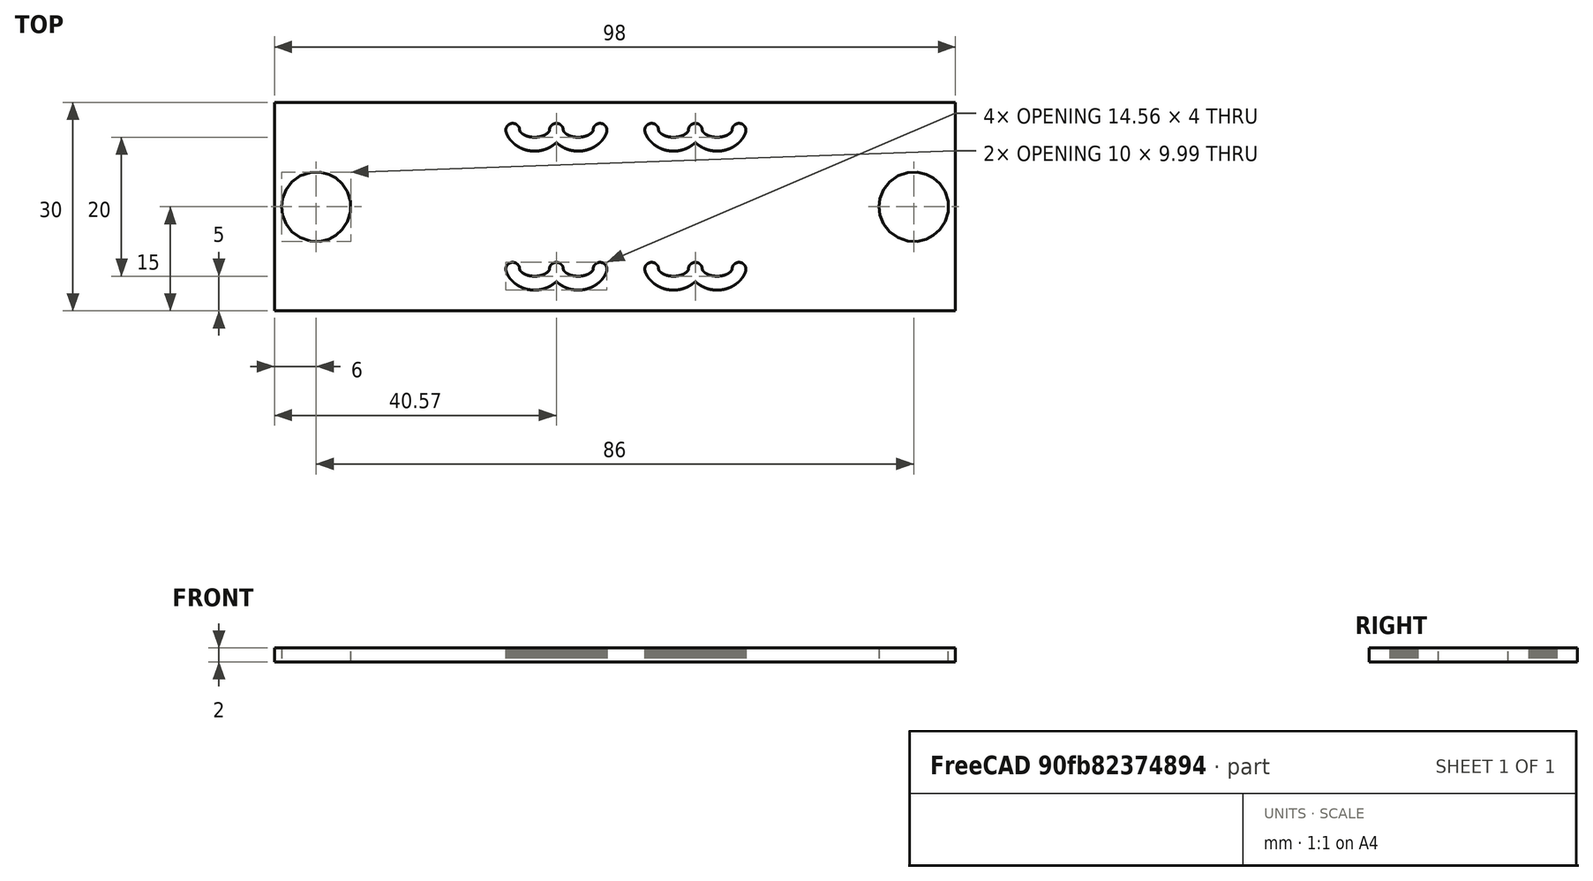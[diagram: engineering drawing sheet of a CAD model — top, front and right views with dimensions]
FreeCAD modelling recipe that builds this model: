
FCSTD DOCUMENT  (FreeCAD 0.21R33771 (Git))
Label: slot
License: All rights reserved
LicenseURL: http://en.wikipedia.org/wiki/All_rights_reserved
objects: Part::Feature×7, PartDesign::CoordinateSystem×2, Sketcher::SketchObject×1, PartDesign::Pad×1, PartDesign::Body×1, App::Part×1, Part::FeaturePython×1
note: 14 computed .brp shape members not serialized (recipe doc carries the construction recipe); baked Part::Feature solids carry a one-line shape summary decoded from their .brp

FEATURE [PartDesign::CoordinateSystem] LCS_0
  AttacherType = Attacher::AttachEngine3D
  MapMode = 2
  Support = -> [X_Axis]
FEATURE [PartDesign::CoordinateSystem] LCS_001
  AttacherType = Attacher::AttachEngine3D
  MapMode = 2
  Support = -> [X_Axis001]
FEATURE [Part::Feature] Rectangle
  shape: bbox 98 x 30 x 2e-07 mm, 0 faces, 0 solids (baked)
FEATURE [Part::Feature] Circle
  Placement = pos=(6,-15,0) rot=(0,0,1;0rad)
  shape: bbox 11.04 x 12.07 x 2e-07 mm, 0 faces, 0 solids (baked)
FEATURE [Part::Feature] Circle001
  Placement = pos=(92,-15,0) rot=(0,0,1;0rad)
  shape: bbox 11.04 x 12.07 x 2e-07 mm, 0 faces, 0 solids (baked)
FEATURE [Part::Feature] Polyline
  shape: bbox 14.56 x 4 x 2e-07 mm, 0 faces, 0 solids (baked)
FEATURE [Part::Feature] Polyline001
  shape: bbox 14.56 x 4 x 2e-07 mm, 0 faces, 0 solids (baked)
FEATURE [Part::Feature] Polyline002
  shape: bbox 14.56 x 4 x 2e-07 mm, 0 faces, 0 solids (baked)
FEATURE [Part::Feature] Polyline003
  shape: bbox 14.56 x 4 x 2e-07 mm, 0 faces, 0 solids (baked)
FEATURE [Sketcher::SketchObject] Sketch
  FullyConstrained = false
  Placement = pos=(0,0,0) rot=(0,0,1;3.14159rad)
  sketch-geometry (1250):
    g0: BSplineCurve PolesCount=2 KnotsCount=2 Degree=1 IsPeriodic=0
    g1: BSplineCurve PolesCount=2 KnotsCount=2 Degree=1 IsPeriodic=0
    g2: BSplineCurve PolesCount=2 KnotsCount=2 Degree=1 IsPeriodic=0
    g3: BSplineCurve PolesCount=2 KnotsCount=2 Degree=1 IsPeriodic=0
    g4: BSplineCurve PolesCount=6 KnotsCount=4 Degree=2 IsPeriodic=1
    g5: BSplineCurve PolesCount=6 KnotsCount=4 Degree=2 IsPeriodic=1
    g6: BSplineCurve PolesCount=2 KnotsCount=2 Degree=1 IsPeriodic=0
    g7: BSplineCurve PolesCount=2 KnotsCount=2 Degree=1 IsPeriodic=0
    g8: BSplineCurve PolesCount=2 KnotsCount=2 Degree=1 IsPeriodic=0
    g9: BSplineCurve PolesCount=2 KnotsCount=2 Degree=1 IsPeriodic=0
    g10: BSplineCurve PolesCount=2 KnotsCount=2 Degree=1 IsPeriodic=0
    g11: BSplineCurve PolesCount=2 KnotsCount=2 Degree=1 IsPeriodic=0
    g12: BSplineCurve PolesCount=2 KnotsCount=2 Degree=1 IsPeriodic=0
    g13: BSplineCurve PolesCount=2 KnotsCount=2 Degree=1 IsPeriodic=0
    g14: BSplineCurve PolesCount=2 KnotsCount=2 Degree=1 IsPeriodic=0
    g15: BSplineCurve PolesCount=2 KnotsCount=2 Degree=1 IsPeriodic=0
    g16: BSplineCurve PolesCount=2 KnotsCount=2 Degree=1 IsPeriodic=0
    g17: BSplineCurve PolesCount=2 KnotsCount=2 Degree=1 IsPeriodic=0
    g18: BSplineCurve PolesCount=2 KnotsCount=2 Degree=1 IsPeriodic=0
    g19: BSplineCurve PolesCount=2 KnotsCount=2 Degree=1 IsPeriodic=0
    g20: BSplineCurve PolesCount=2 KnotsCount=2 Degree=1 IsPeriodic=0
    g21: BSplineCurve PolesCount=2 KnotsCount=2 Degree=1 IsPeriodic=0
    g22: BSplineCurve PolesCount=2 KnotsCount=2 Degree=1 IsPeriodic=0
    g23: BSplineCurve PolesCount=2 KnotsCount=2 Degree=1 IsPeriodic=0
    g24: BSplineCurve PolesCount=2 KnotsCount=2 Degree=1 IsPeriodic=0
    g25: BSplineCurve PolesCount=2 KnotsCount=2 Degree=1 IsPeriodic=0
    g26: BSplineCurve PolesCount=2 KnotsCount=2 Degree=1 IsPeriodic=0
    g27: BSplineCurve PolesCount=2 KnotsCount=2 Degree=1 IsPeriodic=0
    g28: BSplineCurve PolesCount=2 KnotsCount=2 Degree=1 IsPeriodic=0
    g29: BSplineCurve PolesCount=2 KnotsCount=2 Degree=1 IsPeriodic=0
    g30: BSplineCurve PolesCount=2 KnotsCount=2 Degree=1 IsPeriodic=0
    g31: BSplineCurve PolesCount=2 KnotsCount=2 Degree=1 IsPeriodic=0
    g32: BSplineCurve PolesCount=2 KnotsCount=2 Degree=1 IsPeriodic=0
    g33: BSplineCurve PolesCount=2 KnotsCount=2 Degree=1 IsPeriodic=0
    g34: BSplineCurve PolesCount=2 KnotsCount=2 Degree=1 IsPeriodic=0
    g35: BSplineCurve PolesCount=2 KnotsCount=2 Degree=1 IsPeriodic=0
    g36: BSplineCurve PolesCount=2 KnotsCount=2 Degree=1 IsPeriodic=0
    g37: BSplineCurve PolesCount=2 KnotsCount=2 Degree=1 IsPeriodic=0
    g38: BSplineCurve PolesCount=2 KnotsCount=2 Degree=1 IsPeriodic=0
    g39: BSplineCurve PolesCount=2 KnotsCount=2 Degree=1 IsPeriodic=0
    g40: BSplineCurve PolesCount=2 KnotsCount=2 Degree=1 IsPeriodic=0
    g41: BSplineCurve PolesCount=2 KnotsCount=2 Degree=1 IsPeriodic=0
    g42: BSplineCurve PolesCount=2 KnotsCount=2 Degree=1 IsPeriodic=0
    g43: BSplineCurve PolesCount=2 KnotsCount=2 Degree=1 IsPeriodic=0
    g44: BSplineCurve PolesCount=2 KnotsCount=2 Degree=1 IsPeriodic=0
    g45: BSplineCurve PolesCount=2 KnotsCount=2 Degree=1 IsPeriodic=0
    g46: BSplineCurve PolesCount=2 KnotsCount=2 Degree=1 IsPeriodic=0
    g47: BSplineCurve PolesCount=2 KnotsCount=2 Degree=1 IsPeriodic=0
    g48: BSplineCurve PolesCount=2 KnotsCount=2 Degree=1 IsPeriodic=0
    g49: BSplineCurve PolesCount=2 KnotsCount=2 Degree=1 IsPeriodic=0
    g50: BSplineCurve PolesCount=2 KnotsCount=2 Degree=1 IsPeriodic=0
    g51: BSplineCurve PolesCount=2 KnotsCount=2 Degree=1 IsPeriodic=0
    g52: BSplineCurve PolesCount=2 KnotsCount=2 Degree=1 IsPeriodic=0
    g53: BSplineCurve PolesCount=2 KnotsCount=2 Degree=1 IsPeriodic=0
    g54: BSplineCurve PolesCount=2 KnotsCount=2 Degree=1 IsPeriodic=0
    g55: BSplineCurve PolesCount=2 KnotsCount=2 Degree=1 IsPeriodic=0
    g56: BSplineCurve PolesCount=2 KnotsCount=2 Degree=1 IsPeriodic=0
    g57: BSplineCurve PolesCount=2 KnotsCount=2 Degree=1 IsPeriodic=0
    g58: BSplineCurve PolesCount=2 KnotsCount=2 Degree=1 IsPeriodic=0
    g59: BSplineCurve PolesCount=2 KnotsCount=2 Degree=1 IsPeriodic=0
    g60: BSplineCurve PolesCount=2 KnotsCount=2 Degree=1 IsPeriodic=0
    g61: BSplineCurve PolesCount=2 KnotsCount=2 Degree=1 IsPeriodic=0
    g62: BSplineCurve PolesCount=2 KnotsCount=2 Degree=1 IsPeriodic=0
    g63: BSplineCurve PolesCount=2 KnotsCount=2 Degree=1 IsPeriodic=0
    g64: BSplineCurve PolesCount=2 KnotsCount=2 Degree=1 IsPeriodic=0
    g65: BSplineCurve PolesCount=2 KnotsCount=2 Degree=1 IsPeriodic=0
    g66: BSplineCurve PolesCount=2 KnotsCount=2 Degree=1 IsPeriodic=0
    g67: BSplineCurve PolesCount=2 KnotsCount=2 Degree=1 IsPeriodic=0
    g68: BSplineCurve PolesCount=2 KnotsCount=2 Degree=1 IsPeriodic=0
    g69: BSplineCurve PolesCount=2 KnotsCount=2 Degree=1 IsPeriodic=0
    g70: BSplineCurve PolesCount=2 KnotsCount=2 Degree=1 IsPeriodic=0
    g71: BSplineCurve PolesCount=2 KnotsCount=2 Degree=1 IsPeriodic=0
    g72: BSplineCurve PolesCount=2 KnotsCount=2 Degree=1 IsPeriodic=0
    g73: BSplineCurve PolesCount=2 KnotsCount=2 Degree=1 IsPeriodic=0
    g74: BSplineCurve PolesCount=2 KnotsCount=2 Degree=1 IsPeriodic=0
    g75: BSplineCurve PolesCount=2 KnotsCount=2 Degree=1 IsPeriodic=0
    g76: BSplineCurve PolesCount=2 KnotsCount=2 Degree=1 IsPeriodic=0
    g77: BSplineCurve PolesCount=2 KnotsCount=2 Degree=1 IsPeriodic=0
    g78: BSplineCurve PolesCount=2 KnotsCount=2 Degree=1 IsPeriodic=0
    g79: BSplineCurve PolesCount=2 KnotsCount=2 Degree=1 IsPeriodic=0
    g80: BSplineCurve PolesCount=2 KnotsCount=2 Degree=1 IsPeriodic=0
    g81: BSplineCurve PolesCount=2 KnotsCount=2 Degree=1 IsPeriodic=0
    g82: BSplineCurve PolesCount=2 KnotsCount=2 Degree=1 IsPeriodic=0
    g83: BSplineCurve PolesCount=2 KnotsCount=2 Degree=1 IsPeriodic=0
    g84: BSplineCurve PolesCount=2 KnotsCount=2 Degree=1 IsPeriodic=0
    g85: BSplineCurve PolesCount=2 KnotsCount=2 Degree=1 IsPeriodic=0
    g86: BSplineCurve PolesCount=2 KnotsCount=2 Degree=1 IsPeriodic=0
    g87: BSplineCurve PolesCount=2 KnotsCount=2 Degree=1 IsPeriodic=0
    g88: BSplineCurve PolesCount=2 KnotsCount=2 Degree=1 IsPeriodic=0
    g89: BSplineCurve PolesCount=2 KnotsCount=2 Degree=1 IsPeriodic=0
    g90: BSplineCurve PolesCount=2 KnotsCount=2 Degree=1 IsPeriodic=0
    g91: BSplineCurve PolesCount=2 KnotsCount=2 Degree=1 IsPeriodic=0
    g92: BSplineCurve PolesCount=2 KnotsCount=2 Degree=1 IsPeriodic=0
    g93: BSplineCurve PolesCount=2 KnotsCount=2 Degree=1 IsPeriodic=0
    g94: BSplineCurve PolesCount=2 KnotsCount=2 Degree=1 IsPeriodic=0
    g95: BSplineCurve PolesCount=2 KnotsCount=2 Degree=1 IsPeriodic=0
    g96: BSplineCurve PolesCount=2 KnotsCount=2 Degree=1 IsPeriodic=0
    g97: BSplineCurve PolesCount=2 KnotsCount=2 Degree=1 IsPeriodic=0
    g98: BSplineCurve PolesCount=2 KnotsCount=2 Degree=1 IsPeriodic=0
    g99: BSplineCurve PolesCount=2 KnotsCount=2 Degree=1 IsPeriodic=0
    g100: BSplineCurve PolesCount=2 KnotsCount=2 Degree=1 IsPeriodic=0
    g101: BSplineCurve PolesCount=2 KnotsCount=2 Degree=1 IsPeriodic=0
    g102: BSplineCurve PolesCount=2 KnotsCount=2 Degree=1 IsPeriodic=0
    g103: BSplineCurve PolesCount=2 KnotsCount=2 Degree=1 IsPeriodic=0
    g104: BSplineCurve PolesCount=2 KnotsCount=2 Degree=1 IsPeriodic=0
    g105: BSplineCurve PolesCount=2 KnotsCount=2 Degree=1 IsPeriodic=0
    g106: BSplineCurve PolesCount=2 KnotsCount=2 Degree=1 IsPeriodic=0
    g107: BSplineCurve PolesCount=2 KnotsCount=2 Degree=1 IsPeriodic=0
    g108: BSplineCurve PolesCount=2 KnotsCount=2 Degree=1 IsPeriodic=0
    g109: BSplineCurve PolesCount=2 KnotsCount=2 Degree=1 IsPeriodic=0
    g110: BSplineCurve PolesCount=2 KnotsCount=2 Degree=1 IsPeriodic=0
    g111: BSplineCurve PolesCount=2 KnotsCount=2 Degree=1 IsPeriodic=0
    g112: BSplineCurve PolesCount=2 KnotsCount=2 Degree=1 IsPeriodic=0
    g113: BSplineCurve PolesCount=2 KnotsCount=2 Degree=1 IsPeriodic=0
    g114: BSplineCurve PolesCount=2 KnotsCount=2 Degree=1 IsPeriodic=0
    g115: BSplineCurve PolesCount=2 KnotsCount=2 Degree=1 IsPeriodic=0
    g116: BSplineCurve PolesCount=2 KnotsCount=2 Degree=1 IsPeriodic=0
    g117: BSplineCurve PolesCount=2 KnotsCount=2 Degree=1 IsPeriodic=0
    g118: BSplineCurve PolesCount=2 KnotsCount=2 Degree=1 IsPeriodic=0
    g119: BSplineCurve PolesCount=2 KnotsCount=2 Degree=1 IsPeriodic=0
    g120: BSplineCurve PolesCount=2 KnotsCount=2 Degree=1 IsPeriodic=0
    g121: BSplineCurve PolesCount=2 KnotsCount=2 Degree=1 IsPeriodic=0
    g122: BSplineCurve PolesCount=2 KnotsCount=2 Degree=1 IsPeriodic=0
    g123: BSplineCurve PolesCount=2 KnotsCount=2 Degree=1 IsPeriodic=0
    g124: BSplineCurve PolesCount=2 KnotsCount=2 Degree=1 IsPeriodic=0
    g125: BSplineCurve PolesCount=2 KnotsCount=2 Degree=1 IsPeriodic=0
    g126: BSplineCurve PolesCount=2 KnotsCount=2 Degree=1 IsPeriodic=0
    g127: BSplineCurve PolesCount=2 KnotsCount=2 Degree=1 IsPeriodic=0
    g128: BSplineCurve PolesCount=2 KnotsCount=2 Degree=1 IsPeriodic=0
    g129: BSplineCurve PolesCount=2 KnotsCount=2 Degree=1 IsPeriodic=0
    g130: BSplineCurve PolesCount=2 KnotsCount=2 Degree=1 IsPeriodic=0
    g131: BSplineCurve PolesCount=2 KnotsCount=2 Degree=1 IsPeriodic=0
    g132: BSplineCurve PolesCount=2 KnotsCount=2 Degree=1 IsPeriodic=0
    g133: BSplineCurve PolesCount=2 KnotsCount=2 Degree=1 IsPeriodic=0
    g134: BSplineCurve PolesCount=2 KnotsCount=2 Degree=1 IsPeriodic=0
    g135: BSplineCurve PolesCount=2 KnotsCount=2 Degree=1 IsPeriodic=0
    g136: BSplineCurve PolesCount=2 KnotsCount=2 Degree=1 IsPeriodic=0
    g137: BSplineCurve PolesCount=2 KnotsCount=2 Degree=1 IsPeriodic=0
    g138: BSplineCurve PolesCount=2 KnotsCount=2 Degree=1 IsPeriodic=0
    g139: BSplineCurve PolesCount=2 KnotsCount=2 Degree=1 IsPeriodic=0
    g140: BSplineCurve PolesCount=2 KnotsCount=2 Degree=1 IsPeriodic=0
    g141: BSplineCurve PolesCount=2 KnotsCount=2 Degree=1 IsPeriodic=0
    g142: BSplineCurve PolesCount=2 KnotsCount=2 Degree=1 IsPeriodic=0
    g143: BSplineCurve PolesCount=2 KnotsCount=2 Degree=1 IsPeriodic=0
    g144: BSplineCurve PolesCount=2 KnotsCount=2 Degree=1 IsPeriodic=0
    g145: BSplineCurve PolesCount=2 KnotsCount=2 Degree=1 IsPeriodic=0
    g146: BSplineCurve PolesCount=2 KnotsCount=2 Degree=1 IsPeriodic=0
    g147: BSplineCurve PolesCount=2 KnotsCount=2 Degree=1 IsPeriodic=0
    g148: BSplineCurve PolesCount=2 KnotsCount=2 Degree=1 IsPeriodic=0
    g149: BSplineCurve PolesCount=2 KnotsCount=2 Degree=1 IsPeriodic=0
    g150: BSplineCurve PolesCount=2 KnotsCount=2 Degree=1 IsPeriodic=0
    g151: BSplineCurve PolesCount=2 KnotsCount=2 Degree=1 IsPeriodic=0
    g152: BSplineCurve PolesCount=2 KnotsCount=2 Degree=1 IsPeriodic=0
    g153: BSplineCurve PolesCount=2 KnotsCount=2 Degree=1 IsPeriodic=0
    g154: BSplineCurve PolesCount=2 KnotsCount=2 Degree=1 IsPeriodic=0
    g155: BSplineCurve PolesCount=2 KnotsCount=2 Degree=1 IsPeriodic=0
    g156: BSplineCurve PolesCount=2 KnotsCount=2 Degree=1 IsPeriodic=0
    g157: BSplineCurve PolesCount=2 KnotsCount=2 Degree=1 IsPeriodic=0
    g158: BSplineCurve PolesCount=2 KnotsCount=2 Degree=1 IsPeriodic=0
    g159: BSplineCurve PolesCount=2 KnotsCount=2 Degree=1 IsPeriodic=0
    g160: BSplineCurve PolesCount=2 KnotsCount=2 Degree=1 IsPeriodic=0
    g161: BSplineCurve PolesCount=2 KnotsCount=2 Degree=1 IsPeriodic=0
    g162: BSplineCurve PolesCount=2 KnotsCount=2 Degree=1 IsPeriodic=0
    g163: BSplineCurve PolesCount=2 KnotsCount=2 Degree=1 IsPeriodic=0
    g164: BSplineCurve PolesCount=2 KnotsCount=2 Degree=1 IsPeriodic=0
    g165: BSplineCurve PolesCount=2 KnotsCount=2 Degree=1 IsPeriodic=0
    g166: BSplineCurve PolesCount=2 KnotsCount=2 Degree=1 IsPeriodic=0
    g167: BSplineCurve PolesCount=2 KnotsCount=2 Degree=1 IsPeriodic=0
    g168: BSplineCurve PolesCount=2 KnotsCount=2 Degree=1 IsPeriodic=0
    g169: BSplineCurve PolesCount=2 KnotsCount=2 Degree=1 IsPeriodic=0
    g170: BSplineCurve PolesCount=2 KnotsCount=2 Degree=1 IsPeriodic=0
    g171: BSplineCurve PolesCount=2 KnotsCount=2 Degree=1 IsPeriodic=0
    g172: BSplineCurve PolesCount=2 KnotsCount=2 Degree=1 IsPeriodic=0
    g173: BSplineCurve PolesCount=2 KnotsCount=2 Degree=1 IsPeriodic=0
    g174: BSplineCurve PolesCount=2 KnotsCount=2 Degree=1 IsPeriodic=0
    g175: BSplineCurve PolesCount=2 KnotsCount=2 Degree=1 IsPeriodic=0
    g176: BSplineCurve PolesCount=2 KnotsCount=2 Degree=1 IsPeriodic=0
    g177: BSplineCurve PolesCount=2 KnotsCount=2 Degree=1 IsPeriodic=0
    g178: BSplineCurve PolesCount=2 KnotsCount=2 Degree=1 IsPeriodic=0
    g179: BSplineCurve PolesCount=2 KnotsCount=2 Degree=1 IsPeriodic=0
    g180: BSplineCurve PolesCount=2 KnotsCount=2 Degree=1 IsPeriodic=0
    g181: BSplineCurve PolesCount=2 KnotsCount=2 Degree=1 IsPeriodic=0
    g182: BSplineCurve PolesCount=2 KnotsCount=2 Degree=1 IsPeriodic=0
    g183: BSplineCurve PolesCount=2 KnotsCount=2 Degree=1 IsPeriodic=0
    g184: BSplineCurve PolesCount=2 KnotsCount=2 Degree=1 IsPeriodic=0
    g185: BSplineCurve PolesCount=2 KnotsCount=2 Degree=1 IsPeriodic=0
    g186: BSplineCurve PolesCount=2 KnotsCount=2 Degree=1 IsPeriodic=0
    g187: BSplineCurve PolesCount=2 KnotsCount=2 Degree=1 IsPeriodic=0
    g188: BSplineCurve PolesCount=2 KnotsCount=2 Degree=1 IsPeriodic=0
    g189: BSplineCurve PolesCount=2 KnotsCount=2 Degree=1 IsPeriodic=0
    g190: BSplineCurve PolesCount=2 KnotsCount=2 Degree=1 IsPeriodic=0
    g191: BSplineCurve PolesCount=2 KnotsCount=2 Degree=1 IsPeriodic=0
    g192: BSplineCurve PolesCount=2 KnotsCount=2 Degree=1 IsPeriodic=0
    g193: BSplineCurve PolesCount=2 KnotsCount=2 Degree=1 IsPeriodic=0
    g194: BSplineCurve PolesCount=2 KnotsCount=2 Degree=1 IsPeriodic=0
    g195: BSplineCurve PolesCount=2 KnotsCount=2 Degree=1 IsPeriodic=0
    g196: BSplineCurve PolesCount=2 KnotsCount=2 Degree=1 IsPeriodic=0
    g197: BSplineCurve PolesCount=2 KnotsCount=2 Degree=1 IsPeriodic=0
    g198: BSplineCurve PolesCount=2 KnotsCount=2 Degree=1 IsPeriodic=0
    g199: BSplineCurve PolesCount=2 KnotsCount=2 Degree=1 IsPeriodic=0
    g200: BSplineCurve PolesCount=2 KnotsCount=2 Degree=1 IsPeriodic=0
    g201: BSplineCurve PolesCount=2 KnotsCount=2 Degree=1 IsPeriodic=0
    g202: BSplineCurve PolesCount=2 KnotsCount=2 Degree=1 IsPeriodic=0
    g203: BSplineCurve PolesCount=2 KnotsCount=2 Degree=1 IsPeriodic=0
    g204: BSplineCurve PolesCount=2 KnotsCount=2 Degree=1 IsPeriodic=0
    g205: BSplineCurve PolesCount=2 KnotsCount=2 Degree=1 IsPeriodic=0
    g206: BSplineCurve PolesCount=2 KnotsCount=2 Degree=1 IsPeriodic=0
    g207: BSplineCurve PolesCount=2 KnotsCount=2 Degree=1 IsPeriodic=0
    g208: BSplineCurve PolesCount=2 KnotsCount=2 Degree=1 IsPeriodic=0
    g209: BSplineCurve PolesCount=2 KnotsCount=2 Degree=1 IsPeriodic=0
    g210: BSplineCurve PolesCount=2 KnotsCount=2 Degree=1 IsPeriodic=0
    g211: BSplineCurve PolesCount=2 KnotsCount=2 Degree=1 IsPeriodic=0
    g212: BSplineCurve PolesCount=2 KnotsCount=2 Degree=1 IsPeriodic=0
    g213: BSplineCurve PolesCount=2 KnotsCount=2 Degree=1 IsPeriodic=0
    g214: BSplineCurve PolesCount=2 KnotsCount=2 Degree=1 IsPeriodic=0
    g215: BSplineCurve PolesCount=2 KnotsCount=2 Degree=1 IsPeriodic=0
    g216: BSplineCurve PolesCount=2 KnotsCount=2 Degree=1 IsPeriodic=0
    g217: BSplineCurve PolesCount=2 KnotsCount=2 Degree=1 IsPeriodic=0
    g218: BSplineCurve PolesCount=2 KnotsCount=2 Degree=1 IsPeriodic=0
    g219: BSplineCurve PolesCount=2 KnotsCount=2 Degree=1 IsPeriodic=0
    g220: BSplineCurve PolesCount=2 KnotsCount=2 Degree=1 IsPeriodic=0
    g221: BSplineCurve PolesCount=2 KnotsCount=2 Degree=1 IsPeriodic=0
    g222: BSplineCurve PolesCount=2 KnotsCount=2 Degree=1 IsPeriodic=0
    g223: BSplineCurve PolesCount=2 KnotsCount=2 Degree=1 IsPeriodic=0
    g224: BSplineCurve PolesCount=2 KnotsCount=2 Degree=1 IsPeriodic=0
    g225: BSplineCurve PolesCount=2 KnotsCount=2 Degree=1 IsPeriodic=0
    g226: BSplineCurve PolesCount=2 KnotsCount=2 Degree=1 IsPeriodic=0
    g227: BSplineCurve PolesCount=2 KnotsCount=2 Degree=1 IsPeriodic=0
    g228: BSplineCurve PolesCount=2 KnotsCount=2 Degree=1 IsPeriodic=0
    g229: BSplineCurve PolesCount=2 KnotsCount=2 Degree=1 IsPeriodic=0
    g230: BSplineCurve PolesCount=2 KnotsCount=2 Degree=1 IsPeriodic=0
    g231: BSplineCurve PolesCount=2 KnotsCount=2 Degree=1 IsPeriodic=0
    g232: BSplineCurve PolesCount=2 KnotsCount=2 Degree=1 IsPeriodic=0
    g233: BSplineCurve PolesCount=2 KnotsCount=2 Degree=1 IsPeriodic=0
    g234: BSplineCurve PolesCount=2 KnotsCount=2 Degree=1 IsPeriodic=0
    g235: BSplineCurve PolesCount=2 KnotsCount=2 Degree=1 IsPeriodic=0
    g236: BSplineCurve PolesCount=2 KnotsCount=2 Degree=1 IsPeriodic=0
    g237: BSplineCurve PolesCount=2 KnotsCount=2 Degree=1 IsPeriodic=0
    g238: BSplineCurve PolesCount=2 KnotsCount=2 Degree=1 IsPeriodic=0
    g239: BSplineCurve PolesCount=2 KnotsCount=2 Degree=1 IsPeriodic=0
    g240: BSplineCurve PolesCount=2 KnotsCount=2 Degree=1 IsPeriodic=0
    g241: BSplineCurve PolesCount=2 KnotsCount=2 Degree=1 IsPeriodic=0
    g242: BSplineCurve PolesCount=2 KnotsCount=2 Degree=1 IsPeriodic=0
    g243: BSplineCurve PolesCount=2 KnotsCount=2 Degree=1 IsPeriodic=0
    g244: BSplineCurve PolesCount=2 KnotsCount=2 Degree=1 IsPeriodic=0
    g245: BSplineCurve PolesCount=2 KnotsCount=2 Degree=1 IsPeriodic=0
    g246: BSplineCurve PolesCount=2 KnotsCount=2 Degree=1 IsPeriodic=0
    g247: BSplineCurve PolesCount=2 KnotsCount=2 Degree=1 IsPeriodic=0
    g248: BSplineCurve PolesCount=2 KnotsCount=2 Degree=1 IsPeriodic=0
    g249: BSplineCurve PolesCount=2 KnotsCount=2 Degree=1 IsPeriodic=0
    g250: BSplineCurve PolesCount=2 KnotsCount=2 Degree=1 IsPeriodic=0
    g251: BSplineCurve PolesCount=2 KnotsCount=2 Degree=1 IsPeriodic=0
    g252: BSplineCurve PolesCount=2 KnotsCount=2 Degree=1 IsPeriodic=0
    g253: BSplineCurve PolesCount=2 KnotsCount=2 Degree=1 IsPeriodic=0
    g254: BSplineCurve PolesCount=2 KnotsCount=2 Degree=1 IsPeriodic=0
    g255: BSplineCurve PolesCount=2 KnotsCount=2 Degree=1 IsPeriodic=0
    g256: BSplineCurve PolesCount=2 KnotsCount=2 Degree=1 IsPeriodic=0
    g257: BSplineCurve PolesCount=2 KnotsCount=2 Degree=1 IsPeriodic=0
    g258: BSplineCurve PolesCount=2 KnotsCount=2 Degree=1 IsPeriodic=0
    g259: BSplineCurve PolesCount=2 KnotsCount=2 Degree=1 IsPeriodic=0
    g260: BSplineCurve PolesCount=2 KnotsCount=2 Degree=1 IsPeriodic=0
    g261: BSplineCurve PolesCount=2 KnotsCount=2 Degree=1 IsPeriodic=0
    g262: BSplineCurve PolesCount=2 KnotsCount=2 Degree=1 IsPeriodic=0
    g263: BSplineCurve PolesCount=2 KnotsCount=2 Degree=1 IsPeriodic=0
    g264: BSplineCurve PolesCount=2 KnotsCount=2 Degree=1 IsPeriodic=0
    g265: BSplineCurve PolesCount=2 KnotsCount=2 Degree=1 IsPeriodic=0
    g266: BSplineCurve PolesCount=2 KnotsCount=2 Degree=1 IsPeriodic=0
    g267: BSplineCurve PolesCount=2 KnotsCount=2 Degree=1 IsPeriodic=0
    g268: BSplineCurve PolesCount=2 KnotsCount=2 Degree=1 IsPeriodic=0
    g269: BSplineCurve PolesCount=2 KnotsCount=2 Degree=1 IsPeriodic=0
    g270: BSplineCurve PolesCount=2 KnotsCount=2 Degree=1 IsPeriodic=0
    g271: BSplineCurve PolesCount=2 KnotsCount=2 Degree=1 IsPeriodic=0
    g272: BSplineCurve PolesCount=2 KnotsCount=2 Degree=1 IsPeriodic=0
    g273: BSplineCurve PolesCount=2 KnotsCount=2 Degree=1 IsPeriodic=0
    g274: BSplineCurve PolesCount=2 KnotsCount=2 Degree=1 IsPeriodic=0
    g275: BSplineCurve PolesCount=2 KnotsCount=2 Degree=1 IsPeriodic=0
    g276: BSplineCurve PolesCount=2 KnotsCount=2 Degree=1 IsPeriodic=0
    g277: BSplineCurve PolesCount=2 KnotsCount=2 Degree=1 IsPeriodic=0
    g278: BSplineCurve PolesCount=2 KnotsCount=2 Degree=1 IsPeriodic=0
    g279: BSplineCurve PolesCount=2 KnotsCount=2 Degree=1 IsPeriodic=0
    g280: BSplineCurve PolesCount=2 KnotsCount=2 Degree=1 IsPeriodic=0
    g281: BSplineCurve PolesCount=2 KnotsCount=2 Degree=1 IsPeriodic=0
    g282: BSplineCurve PolesCount=2 KnotsCount=2 Degree=1 IsPeriodic=0
    g283: BSplineCurve PolesCount=2 KnotsCount=2 Degree=1 IsPeriodic=0
    g284: BSplineCurve PolesCount=2 KnotsCount=2 Degree=1 IsPeriodic=0
    g285: BSplineCurve PolesCount=2 KnotsCount=2 Degree=1 IsPeriodic=0
    g286: BSplineCurve PolesCount=2 KnotsCount=2 Degree=1 IsPeriodic=0
    g287: BSplineCurve PolesCount=2 KnotsCount=2 Degree=1 IsPeriodic=0
    g288: BSplineCurve PolesCount=2 KnotsCount=2 Degree=1 IsPeriodic=0
    g289: BSplineCurve PolesCount=2 KnotsCount=2 Degree=1 IsPeriodic=0
    g290: BSplineCurve PolesCount=2 KnotsCount=2 Degree=1 IsPeriodic=0
    g291: BSplineCurve PolesCount=2 KnotsCount=2 Degree=1 IsPeriodic=0
    g292: BSplineCurve PolesCount=2 KnotsCount=2 Degree=1 IsPeriodic=0
    g293: BSplineCurve PolesCount=2 KnotsCount=2 Degree=1 IsPeriodic=0
    g294: BSplineCurve PolesCount=2 KnotsCount=2 Degree=1 IsPeriodic=0
    g295: BSplineCurve PolesCount=2 KnotsCount=2 Degree=1 IsPeriodic=0
    g296: BSplineCurve PolesCount=2 KnotsCount=2 Degree=1 IsPeriodic=0
    g297: BSplineCurve PolesCount=2 KnotsCount=2 Degree=1 IsPeriodic=0
    g298: BSplineCurve PolesCount=2 KnotsCount=2 Degree=1 IsPeriodic=0
    g299: BSplineCurve PolesCount=2 KnotsCount=2 Degree=1 IsPeriodic=0
    g300: BSplineCurve PolesCount=2 KnotsCount=2 Degree=1 IsPeriodic=0
    g301: BSplineCurve PolesCount=2 KnotsCount=2 Degree=1 IsPeriodic=0
    g302: BSplineCurve PolesCount=2 KnotsCount=2 Degree=1 IsPeriodic=0
    g303: BSplineCurve PolesCount=2 KnotsCount=2 Degree=1 IsPeriodic=0
    g304: BSplineCurve PolesCount=2 KnotsCount=2 Degree=1 IsPeriodic=0
    g305: BSplineCurve PolesCount=2 KnotsCount=2 Degree=1 IsPeriodic=0
    g306: BSplineCurve PolesCount=2 KnotsCount=2 Degree=1 IsPeriodic=0
    g307: BSplineCurve PolesCount=2 KnotsCount=2 Degree=1 IsPeriodic=0
    g308: BSplineCurve PolesCount=2 KnotsCount=2 Degree=1 IsPeriodic=0
    g309: BSplineCurve PolesCount=2 KnotsCount=2 Degree=1 IsPeriodic=0
    g310: BSplineCurve PolesCount=2 KnotsCount=2 Degree=1 IsPeriodic=0
    g311: BSplineCurve PolesCount=2 KnotsCount=2 Degree=1 IsPeriodic=0
    g312: BSplineCurve PolesCount=2 KnotsCount=2 Degree=1 IsPeriodic=0
    g313: BSplineCurve PolesCount=2 KnotsCount=2 Degree=1 IsPeriodic=0
    g314: BSplineCurve PolesCount=2 KnotsCount=2 Degree=1 IsPeriodic=0
    g315: BSplineCurve PolesCount=2 KnotsCount=2 Degree=1 IsPeriodic=0
    g316: BSplineCurve PolesCount=2 KnotsCount=2 Degree=1 IsPeriodic=0
    g317: BSplineCurve PolesCount=2 KnotsCount=2 Degree=1 IsPeriodic=0
    g318: BSplineCurve PolesCount=2 KnotsCount=2 Degree=1 IsPeriodic=0
    g319: BSplineCurve PolesCount=2 KnotsCount=2 Degree=1 IsPeriodic=0
    g320: BSplineCurve PolesCount=2 KnotsCount=2 Degree=1 IsPeriodic=0
    g321: BSplineCurve PolesCount=2 KnotsCount=2 Degree=1 IsPeriodic=0
    g322: BSplineCurve PolesCount=2 KnotsCount=2 Degree=1 IsPeriodic=0
    g323: BSplineCurve PolesCount=2 KnotsCount=2 Degree=1 IsPeriodic=0
    g324: BSplineCurve PolesCount=2 KnotsCount=2 Degree=1 IsPeriodic=0
    g325: BSplineCurve PolesCount=2 KnotsCount=2 Degree=1 IsPeriodic=0
    g326: BSplineCurve PolesCount=2 KnotsCount=2 Degree=1 IsPeriodic=0
    g327: BSplineCurve PolesCount=2 KnotsCount=2 Degree=1 IsPeriodic=0
    g328: BSplineCurve PolesCount=2 KnotsCount=2 Degree=1 IsPeriodic=0
    g329: BSplineCurve PolesCount=2 KnotsCount=2 Degree=1 IsPeriodic=0
    g330: BSplineCurve PolesCount=2 KnotsCount=2 Degree=1 IsPeriodic=0
    g331: BSplineCurve PolesCount=2 KnotsCount=2 Degree=1 IsPeriodic=0
    g332: BSplineCurve PolesCount=2 KnotsCount=2 Degree=1 IsPeriodic=0
    g333: BSplineCurve PolesCount=2 KnotsCount=2 Degree=1 IsPeriodic=0
    g334: BSplineCurve PolesCount=2 KnotsCount=2 Degree=1 IsPeriodic=0
    g335: BSplineCurve PolesCount=2 KnotsCount=2 Degree=1 IsPeriodic=0
    g336: BSplineCurve PolesCount=2 KnotsCount=2 Degree=1 IsPeriodic=0
    g337: BSplineCurve PolesCount=2 KnotsCount=2 Degree=1 IsPeriodic=0
    g338: BSplineCurve PolesCount=2 KnotsCount=2 Degree=1 IsPeriodic=0
    g339: BSplineCurve PolesCount=2 KnotsCount=2 Degree=1 IsPeriodic=0
    g340: BSplineCurve PolesCount=2 KnotsCount=2 Degree=1 IsPeriodic=0
    g341: BSplineCurve PolesCount=2 KnotsCount=2 Degree=1 IsPeriodic=0
    g342: BSplineCurve PolesCount=2 KnotsCount=2 Degree=1 IsPeriodic=0
    g343: BSplineCurve PolesCount=2 KnotsCount=2 Degree=1 IsPeriodic=0
    g344: BSplineCurve PolesCount=2 KnotsCount=2 Degree=1 IsPeriodic=0
    g345: BSplineCurve PolesCount=2 KnotsCount=2 Degree=1 IsPeriodic=0
    g346: BSplineCurve PolesCount=2 KnotsCount=2 Degree=1 IsPeriodic=0
    g347: BSplineCurve PolesCount=2 KnotsCount=2 Degree=1 IsPeriodic=0
    g348: BSplineCurve PolesCount=2 KnotsCount=2 Degree=1 IsPeriodic=0
    g349: BSplineCurve PolesCount=2 KnotsCount=2 Degree=1 IsPeriodic=0
    g350: BSplineCurve PolesCount=2 KnotsCount=2 Degree=1 IsPeriodic=0
    g351: BSplineCurve PolesCount=2 KnotsCount=2 Degree=1 IsPeriodic=0
    g352: BSplineCurve PolesCount=2 KnotsCount=2 Degree=1 IsPeriodic=0
    g353: BSplineCurve PolesCount=2 KnotsCount=2 Degree=1 IsPeriodic=0
    g354: BSplineCurve PolesCount=2 KnotsCount=2 Degree=1 IsPeriodic=0
    g355: BSplineCurve PolesCount=2 KnotsCount=2 Degree=1 IsPeriodic=0
    g356: BSplineCurve PolesCount=2 KnotsCount=2 Degree=1 IsPeriodic=0
    g357: BSplineCurve PolesCount=2 KnotsCount=2 Degree=1 IsPeriodic=0
    g358: BSplineCurve PolesCount=2 KnotsCount=2 Degree=1 IsPeriodic=0
    g359: BSplineCurve PolesCount=2 KnotsCount=2 Degree=1 IsPeriodic=0
    g360: BSplineCurve PolesCount=2 KnotsCount=2 Degree=1 IsPeriodic=0
    g361: BSplineCurve PolesCount=2 KnotsCount=2 Degree=1 IsPeriodic=0
    g362: BSplineCurve PolesCount=2 KnotsCount=2 Degree=1 IsPeriodic=0
    g363: BSplineCurve PolesCount=2 KnotsCount=2 Degree=1 IsPeriodic=0
    g364: BSplineCurve PolesCount=2 KnotsCount=2 Degree=1 IsPeriodic=0
    g365: BSplineCurve PolesCount=2 KnotsCount=2 Degree=1 IsPeriodic=0
    g366: BSplineCurve PolesCount=2 KnotsCount=2 Degree=1 IsPeriodic=0
    g367: BSplineCurve PolesCount=2 KnotsCount=2 Degree=1 IsPeriodic=0
    g368: BSplineCurve PolesCount=2 KnotsCount=2 Degree=1 IsPeriodic=0
    g369: BSplineCurve PolesCount=2 KnotsCount=2 Degree=1 IsPeriodic=0
    g370: BSplineCurve PolesCount=2 KnotsCount=2 Degree=1 IsPeriodic=0
    g371: BSplineCurve PolesCount=2 KnotsCount=2 Degree=1 IsPeriodic=0
    g372: BSplineCurve PolesCount=2 KnotsCount=2 Degree=1 IsPeriodic=0
    g373: BSplineCurve PolesCount=2 KnotsCount=2 Degree=1 IsPeriodic=0
    g374: BSplineCurve PolesCount=2 KnotsCount=2 Degree=1 IsPeriodic=0
    g375: BSplineCurve PolesCount=2 KnotsCount=2 Degree=1 IsPeriodic=0
    g376: BSplineCurve PolesCount=2 KnotsCount=2 Degree=1 IsPeriodic=0
    g377: BSplineCurve PolesCount=2 KnotsCount=2 Degree=1 IsPeriodic=0
    g378: BSplineCurve PolesCount=2 KnotsCount=2 Degree=1 IsPeriodic=0
    g379: BSplineCurve PolesCount=2 KnotsCount=2 Degree=1 IsPeriodic=0
    g380: BSplineCurve PolesCount=2 KnotsCount=2 Degree=1 IsPeriodic=0
    g381: BSplineCurve PolesCount=2 KnotsCount=2 Degree=1 IsPeriodic=0
    g382: BSplineCurve PolesCount=2 KnotsCount=2 Degree=1 IsPeriodic=0
    g383: BSplineCurve PolesCount=2 KnotsCount=2 Degree=1 IsPeriodic=0
    g384: BSplineCurve PolesCount=2 KnotsCount=2 Degree=1 IsPeriodic=0
    g385: BSplineCurve PolesCount=2 KnotsCount=2 Degree=1 IsPeriodic=0
    g386: BSplineCurve PolesCount=2 KnotsCount=2 Degree=1 IsPeriodic=0
    g387: BSplineCurve PolesCount=2 KnotsCount=2 Degree=1 IsPeriodic=0
    g388: BSplineCurve PolesCount=2 KnotsCount=2 Degree=1 IsPeriodic=0
    g389: BSplineCurve PolesCount=2 KnotsCount=2 Degree=1 IsPeriodic=0
    g390: BSplineCurve PolesCount=2 KnotsCount=2 Degree=1 IsPeriodic=0
    g391: BSplineCurve PolesCount=2 KnotsCount=2 Degree=1 IsPeriodic=0
    g392: BSplineCurve PolesCount=2 KnotsCount=2 Degree=1 IsPeriodic=0
    g393: BSplineCurve PolesCount=2 KnotsCount=2 Degree=1 IsPeriodic=0
    g394: BSplineCurve PolesCount=2 KnotsCount=2 Degree=1 IsPeriodic=0
    g395: BSplineCurve PolesCount=2 KnotsCount=2 Degree=1 IsPeriodic=0
    g396: BSplineCurve PolesCount=2 KnotsCount=2 Degree=1 IsPeriodic=0
    g397: BSplineCurve PolesCount=2 KnotsCount=2 Degree=1 IsPeriodic=0
    g398: BSplineCurve PolesCount=2 KnotsCount=2 Degree=1 IsPeriodic=0
    g399: BSplineCurve PolesCount=2 KnotsCount=2 Degree=1 IsPeriodic=0
    ... +850 more geometry lines
  constraints (1248):
    c: Coincident(g0,g1)
    c: Coincident(g1,g2)
    c: Coincident(g2,g3)
    c: Coincident(g3,g0)
    c: Coincident(g6,g7)
    c: Coincident(g7,g8)
    c: Coincident(g8,g9)
    c: Coincident(g9,g10)
    c: Coincident(g10,g11)
    c: Coincident(g11,g12)
    c: Coincident(g12,g13)
    c: Coincident(g13,g14)
    c: Coincident(g14,g15)
    c: Coincident(g15,g16)
    c: Coincident(g16,g17)
    c: Coincident(g17,g18)
    c: Coincident(g18,g19)
    c: Coincident(g19,g20)
    c: Coincident(g20,g21)
    c: Coincident(g21,g22)
    c: Coincident(g22,g23)
    c: Coincident(g23,g24)
    c: Coincident(g24,g25)
    c: Coincident(g25,g26)
    c: Coincident(g26,g27)
    c: Coincident(g27,g28)
    c: Coincident(g28,g29)
    c: Coincident(g29,g30)
    c: Coincident(g30,g31)
    c: Coincident(g31,g32)
    c: Coincident(g32,g33)
    c: Coincident(g33,g34)
    c: Coincident(g34,g35)
    c: Coincident(g35,g36)
    c: Coincident(g36,g37)
    c: Coincident(g37,g38)
    c: Coincident(g38,g39)
    c: Coincident(g39,g40)
    c: Coincident(g40,g41)
    c: Coincident(g41,g42)
    c: Coincident(g42,g43)
    c: Coincident(g43,g44)
    c: Coincident(g44,g45)
    c: Coincident(g45,g46)
    c: Coincident(g46,g47)
    c: Coincident(g47,g48)
    c: Coincident(g48,g49)
    c: Coincident(g49,g50)
    c: Coincident(g50,g51)
    c: Coincident(g51,g52)
    c: Coincident(g52,g53)
    c: Coincident(g53,g54)
    c: Coincident(g54,g55)
    c: Coincident(g55,g56)
    c: Coincident(g56,g57)
    c: Coincident(g57,g58)
    c: Coincident(g58,g59)
    c: Coincident(g59,g60)
    c: Coincident(g60,g61)
    c: Coincident(g61,g62)
    c: Coincident(g62,g63)
    c: Coincident(g63,g64)
    c: Coincident(g64,g65)
    c: Coincident(g65,g66)
    c: Coincident(g66,g67)
    c: Coincident(g67,g68)
    c: Coincident(g68,g69)
    c: Coincident(g69,g70)
    c: Coincident(g70,g71)
    c: Coincident(g71,g72)
    c: Coincident(g72,g73)
    c: Coincident(g73,g74)
    c: Coincident(g74,g75)
    c: Coincident(g75,g76)
    c: Coincident(g76,g77)
    c: Coincident(g77,g78)
    c: Coincident(g78,g79)
    c: Coincident(g79,g80)
    c: Coincident(g80,g81)
    c: Coincident(g81,g82)
    c: Coincident(g82,g83)
    c: Coincident(g83,g84)
    c: Coincident(g84,g85)
    c: Coincident(g85,g86)
    c: Coincident(g86,g87)
    c: Coincident(g87,g88)
    c: Coincident(g88,g89)
    c: Coincident(g89,g90)
    c: Coincident(g90,g91)
    c: Coincident(g91,g92)
    c: Coincident(g92,g93)
    c: Coincident(g93,g94)
    c: Coincident(g94,g95)
    c: Coincident(g95,g96)
    c: Coincident(g96,g97)
    c: Coincident(g97,g98)
    c: Coincident(g98,g99)
    c: Coincident(g99,g100)
    c: Coincident(g100,g101)
    c: Coincident(g101,g102)
    c: Coincident(g102,g103)
    c: Coincident(g103,g104)
    c: Coincident(g104,g105)
    c: Coincident(g105,g106)
    c: Coincident(g106,g107)
    c: Coincident(g107,g108)
    c: Coincident(g108,g109)
    c: Coincident(g109,g110)
    c: Coincident(g110,g111)
    c: Coincident(g111,g112)
    c: Coincident(g112,g113)
    c: Coincident(g113,g114)
    c: Coincident(g114,g115)
    c: Coincident(g115,g116)
    c: Coincident(g116,g117)
    c: Coincident(g117,g118)
    c: Coincident(g118,g119)
    c: Coincident(g119,g120)
    c: Coincident(g120,g121)
    c: Coincident(g121,g122)
    c: Coincident(g122,g123)
    c: Coincident(g123,g124)
    c: Coincident(g124,g125)
    c: Coincident(g125,g126)
    c: Coincident(g126,g127)
    c: Coincident(g127,g128)
    c: Coincident(g128,g129)
    c: Coincident(g129,g130)
    c: Coincident(g130,g131)
    c: Coincident(g131,g132)
    c: Coincident(g132,g133)
    c: Coincident(g133,g134)
    c: Coincident(g134,g135)
    c: Coincident(g135,g136)
    c: Coincident(g136,g137)
    c: Coincident(g137,g138)
    c: Coincident(g138,g139)
    c: Coincident(g139,g140)
    c: Coincident(g140,g141)
    c: Coincident(g141,g142)
    c: Coincident(g142,g143)
    c: Coincident(g143,g144)
    c: Coincident(g144,g145)
    c: Coincident(g145,g146)
    c: Coincident(g146,g147)
    c: Coincident(g147,g148)
    c: Coincident(g148,g149)
    c: Coincident(g149,g150)
    c: Coincident(g150,g151)
    c: Coincident(g151,g152)
    c: Coincident(g152,g153)
    c: Coincident(g153,g154)
    c: Coincident(g154,g155)
    c: Coincident(g155,g156)
    c: Coincident(g156,g157)
    c: Coincident(g157,g158)
    c: Coincident(g158,g159)
    c: Coincident(g159,g160)
    c: Coincident(g160,g161)
    c: Coincident(g161,g162)
    c: Coincident(g162,g163)
    c: Coincident(g163,g164)
    c: Coincident(g164,g165)
    c: Coincident(g165,g166)
    c: Coincident(g166,g167)
    c: Coincident(g167,g168)
    c: Coincident(g168,g169)
    c: Coincident(g169,g170)
    c: Coincident(g170,g171)
    c: Coincident(g171,g172)
    c: Coincident(g172,g173)
    c: Coincident(g173,g174)
    c: Coincident(g174,g175)
    c: Coincident(g175,g176)
    c: Coincident(g176,g177)
    c: Coincident(g177,g178)
    c: Coincident(g178,g179)
    c: Coincident(g179,g180)
    c: Coincident(g180,g181)
    c: Coincident(g181,g182)
    c: Coincident(g182,g183)
    c: Coincident(g183,g184)
    c: Coincident(g184,g185)
    c: Coincident(g185,g186)
    c: Coincident(g186,g187)
    c: Coincident(g187,g188)
    c: Coincident(g188,g189)
    c: Coincident(g189,g190)
    c: Coincident(g190,g191)
    c: Coincident(g191,g192)
    c: Coincident(g192,g193)
    c: Coincident(g193,g194)
    c: Coincident(g194,g195)
    c: Coincident(g195,g196)
    c: Coincident(g196,g197)
    c: Coincident(g197,g198)
    c: Coincident(g198,g199)
    c: Coincident(g199,g200)
    c: Coincident(g200,g201)
    c: Coincident(g201,g202)
    c: Coincident(g202,g203)
    c: Coincident(g203,g204)
    c: Coincident(g204,g205)
    c: Coincident(g205,g206)
    c: Coincident(g206,g207)
    c: Coincident(g207,g208)
    c: Coincident(g208,g209)
    c: Coincident(g209,g210)
    c: Coincident(g210,g211)
    c: Coincident(g211,g212)
    c: Coincident(g212,g213)
    c: Coincident(g213,g214)
    c: Coincident(g214,g215)
    c: Coincident(g215,g216)
    c: Coincident(g216,g217)
    c: Coincident(g217,g218)
    c: Coincident(g218,g219)
    c: Coincident(g219,g220)
    c: Coincident(g220,g221)
    c: Coincident(g221,g222)
    c: Coincident(g222,g223)
    c: Coincident(g223,g224)
    c: Coincident(g224,g225)
    c: Coincident(g225,g226)
    c: Coincident(g226,g227)
    c: Coincident(g227,g228)
    c: Coincident(g228,g229)
    c: Coincident(g229,g230)
    c: Coincident(g230,g231)
    c: Coincident(g231,g232)
    c: Coincident(g232,g233)
    c: Coincident(g233,g234)
    c: Coincident(g234,g235)
    c: Coincident(g235,g236)
    c: Coincident(g236,g237)
    c: Coincident(g237,g238)
    c: Coincident(g238,g239)
    c: Coincident(g239,g240)
    c: Coincident(g240,g241)
    c: Coincident(g241,g242)
    c: Coincident(g242,g243)
    c: Coincident(g243,g244)
    c: Coincident(g244,g245)
    c: Coincident(g245,g246)
    c: Coincident(g246,g247)
    c: Coincident(g247,g248)
    c: Coincident(g248,g249)
    c: Coincident(g249,g250)
    c: Coincident(g250,g251)
    c: Coincident(g251,g252)
    c: Coincident(g252,g253)
    c: Coincident(g253,g254)
    c: Coincident(g254,g255)
    c: Coincident(g255,g256)
    c: Coincident(g256,g257)
    c: Coincident(g257,g258)
    c: Coincident(g258,g259)
    c: Coincident(g259,g260)
    c: Coincident(g260,g261)
    c: Coincident(g261,g262)
    c: Coincident(g262,g263)
    c: Coincident(g263,g264)
    c: Coincident(g264,g265)
    c: Coincident(g265,g266)
    c: Coincident(g266,g267)
    c: Coincident(g267,g268)
    c: Coincident(g268,g269)
    c: Coincident(g269,g270)
    c: Coincident(g270,g271)
    c: Coincident(g271,g272)
    c: Coincident(g272,g273)
    c: Coincident(g273,g274)
    c: Coincident(g274,g275)
    c: Coincident(g275,g276)
    c: Coincident(g276,g277)
    c: Coincident(g277,g278)
    c: Coincident(g278,g279)
    c: Coincident(g279,g280)
    c: Coincident(g280,g281)
    c: Coincident(g281,g282)
    c: Coincident(g282,g283)
    c: Coincident(g283,g284)
    c: Coincident(g284,g285)
    c: Coincident(g285,g286)
    c: Coincident(g286,g287)
    c: Coincident(g287,g288)
    c: Coincident(g288,g289)
    c: Coincident(g289,g290)
    c: Coincident(g290,g291)
    c: Coincident(g291,g292)
    c: Coincident(g292,g293)
    c: Coincident(g293,g294)
    c: Coincident(g294,g295)
    c: Coincident(g295,g296)
    c: Coincident(g296,g297)
    c: Coincident(g297,g298)
    c: Coincident(g298,g299)
    c: Coincident(g299,g300)
    c: Coincident(g300,g301)
    c: Coincident(g301,g302)
    c: Coincident(g302,g303)
    c: Coincident(g303,g304)
    c: Coincident(g304,g305)
    c: Coincident(g305,g306)
    c: Coincident(g306,g307)
    c: Coincident(g307,g308)
    c: Coincident(g308,g309)
    c: Coincident(g309,g310)
    c: Coincident(g310,g311)
    c: Coincident(g311,g312)
    c: Coincident(g312,g313)
    c: Coincident(g313,g314)
    c: Coincident(g314,g315)
    c: Coincident(g315,g316)
    c: Coincident(g316,g6)
    c: Coincident(g317,g318)
    c: Coincident(g318,g319)
    c: Coincident(g319,g320)
    c: Coincident(g320,g321)
    c: Coincident(g321,g322)
    c: Coincident(g322,g323)
    c: Coincident(g323,g324)
    c: Coincident(g324,g325)
    c: Coincident(g325,g326)
    c: Coincident(g326,g327)
    c: Coincident(g327,g328)
    c: Coincident(g328,g329)
    c: Coincident(g329,g330)
    c: Coincident(g330,g331)
    c: Coincident(g331,g332)
    c: Coincident(g332,g333)
    c: Coincident(g333,g334)
    c: Coincident(g334,g335)
    c: Coincident(g335,g336)
    c: Coincident(g336,g337)
    c: Coincident(g337,g338)
    c: Coincident(g338,g339)
    c: Coincident(g339,g340)
    c: Coincident(g340,g341)
    c: Coincident(g341,g342)
    c: Coincident(g342,g343)
    c: Coincident(g343,g344)
    c: Coincident(g344,g345)
    c: Coincident(g345,g346)
    c: Coincident(g346,g347)
    c: Coincident(g347,g348)
    c: Coincident(g348,g349)
    c: Coincident(g349,g350)
    c: Coincident(g350,g351)
    c: Coincident(g351,g352)
    c: Coincident(g352,g353)
    c: Coincident(g353,g354)
    c: Coincident(g354,g355)
    c: Coincident(g355,g356)
    c: Coincident(g356,g357)
    c: Coincident(g357,g358)
    c: Coincident(g358,g359)
    c: Coincident(g359,g360)
    c: Coincident(g360,g361)
    c: Coincident(g361,g362)
    c: Coincident(g362,g363)
    c: Coincident(g363,g364)
    c: Coincident(g364,g365)
    c: Coincident(g365,g366)
    c: Coincident(g366,g367)
    c: Coincident(g367,g368)
    c: Coincident(g368,g369)
    c: Coincident(g369,g370)
    c: Coincident(g370,g371)
    c: Coincident(g371,g372)
    c: Coincident(g372,g373)
    c: Coincident(g373,g374)
    c: Coincident(g374,g375)
    c: Coincident(g375,g376)
    c: Coincident(g376,g377)
    c: Coincident(g377,g378)
    c: Coincident(g378,g379)
    c: Coincident(g379,g380)
    c: Coincident(g380,g381)
    c: Coincident(g381,g382)
    c: Coincident(g382,g383)
    c: Coincident(g383,g384)
    c: Coincident(g384,g385)
    c: Coincident(g385,g386)
    c: Coincident(g386,g387)
    c: Coincident(g387,g388)
    c: Coincident(g388,g389)
    c: Coincident(g389,g390)
    c: Coincident(g390,g391)
    c: Coincident(g391,g392)
    c: Coincident(g392,g393)
    c: Coincident(g393,g394)
    c: Coincident(g394,g395)
    c: Coincident(g395,g396)
    c: Coincident(g396,g397)
    c: Coincident(g397,g398)
    c: Coincident(g398,g399)
    c: Coincident(g399,g400)
    c: Coincident(g400,g401)
    c: Coincident(g401,g402)
    c: Coincident(g402,g403)
    c: Coincident(g403,g404)
    c: Coincident(g404,g405)
    c: Coincident(g405,g406)
    c: Coincident(g406,g407)
    c: Coincident(g407,g408)
    c: Coincident(g408,g409)
    c: Coincident(g409,g410)
    c: Coincident(g410,g411)
    c: Coincident(g411,g412)
    c: Coincident(g412,g413)
    c: Coincident(g413,g414)
    c: Coincident(g414,g415)
    c: Coincident(g415,g416)
    c: Coincident(g416,g417)
    c: Coincident(g417,g418)
    c: Coincident(g418,g419)
    c: Coincident(g419,g420)
    c: Coincident(g420,g421)
    c: Coincident(g421,g422)
    c: Coincident(g422,g423)
    c: Coincident(g423,g424)
    c: Coincident(g424,g425)
    c: Coincident(g425,g426)
    c: Coincident(g426,g427)
    c: Coincident(g427,g428)
    c: Coincident(g428,g429)
    c: Coincident(g429,g430)
    c: Coincident(g430,g431)
    c: Coincident(g431,g432)
    c: Coincident(g432,g433)
    c: Coincident(g433,g434)
    c: Coincident(g434,g435)
    c: Coincident(g435,g436)
    c: Coincident(g436,g437)
    c: Coincident(g437,g438)
    c: Coincident(g438,g439)
    c: Coincident(g439,g440)
    c: Coincident(g440,g441)
    c: Coincident(g441,g442)
    c: Coincident(g442,g443)
    c: Coincident(g443,g444)
    c: Coincident(g444,g445)
    c: Coincident(g445,g446)
    c: Coincident(g446,g447)
    c: Coincident(g447,g448)
    c: Coincident(g448,g449)
    c: Coincident(g449,g450)
    c: Coincident(g450,g451)
    c: Coincident(g451,g452)
    c: Coincident(g452,g453)
    c: Coincident(g453,g454)
    c: Coincident(g454,g455)
    c: Coincident(g455,g456)
    c: Coincident(g456,g457)
    c: Coincident(g457,g458)
    c: Coincident(g458,g459)
    c: Coincident(g459,g460)
    c: Coincident(g460,g461)
    c: Coincident(g461,g462)
    c: Coincident(g462,g463)
    c: Coincident(g463,g464)
    c: Coincident(g464,g465)
    c: Coincident(g465,g466)
    c: Coincident(g466,g467)
    c: Coincident(g467,g468)
    c: Coincident(g468,g469)
    c: Coincident(g469,g470)
    c: Coincident(g470,g471)
    c: Coincident(g471,g472)
    c: Coincident(g472,g473)
    c: Coincident(g473,g474)
    c: Coincident(g474,g475)
    c: Coincident(g475,g476)
    c: Coincident(g476,g477)
    c: Coincident(g477,g478)
    c: Coincident(g478,g479)
    c: Coincident(g479,g480)
    c: Coincident(g480,g481)
    c: Coincident(g481,g482)
    c: Coincident(g482,g483)
    c: Coincident(g483,g484)
    c: Coincident(g484,g485)
    c: Coincident(g485,g486)
    c: Coincident(g486,g487)
    c: Coincident(g487,g488)
    c: Coincident(g488,g489)
    c: Coincident(g489,g490)
    c: Coincident(g490,g491)
    c: Coincident(g491,g492)
    c: Coincident(g492,g493)
    c: Coincident(g493,g494)
    c: Coincident(g494,g495)
    c: Coincident(g495,g496)
    c: Coincident(g496,g497)
    c: Coincident(g497,g498)
    c: Coincident(g498,g499)
    c: Coincident(g499,g500)
    c: Coincident(g500,g501)
    c: Coincident(g501,g502)
    c: Coincident(g502,g503)
    c: Coincident(g503,g504)
    c: Coincident(g504,g505)
    c: Coincident(g505,g506)
    c: Coincident(g506,g507)
    c: Coincident(g507,g508)
    c: Coincident(g508,g509)
    c: Coincident(g509,g510)
    c: Coincident(g510,g511)
    c: Coincident(g511,g512)
    c: Coincident(g512,g513)
    c: Coincident(g513,g514)
    c: Coincident(g514,g515)
    c: Coincident(g515,g516)
    c: Coincident(g516,g517)
    c: Coincident(g517,g518)
    c: Coincident(g518,g519)
    c: Coincident(g519,g520)
    c: Coincident(g520,g521)
    c: Coincident(g521,g522)
    c: Coincident(g522,g523)
    c: Coincident(g523,g524)
    c: Coincident(g524,g525)
    c: Coincident(g525,g526)
    c: Coincident(g526,g527)
    c: Coincident(g527,g528)
    c: Coincident(g528,g529)
    c: Coincident(g529,g530)
    c: Coincident(g530,g531)
    c: Coincident(g531,g532)
    c: Coincident(g532,g533)
    c: Coincident(g533,g534)
    c: Coincident(g534,g535)
    c: Coincident(g535,g536)
    c: Coincident(g536,g537)
    c: Coincident(g537,g538)
    c: Coincident(g538,g539)
    c: Coincident(g539,g540)
    c: Coincident(g540,g541)
    c: Coincident(g541,g542)
    c: Coincident(g542,g543)
    c: Coincident(g543,g544)
    c: Coincident(g544,g545)
    c: Coincident(g545,g546)
    c: Coincident(g546,g547)
    c: Coincident(g547,g548)
    c: Coincident(g548,g549)
    c: Coincident(g549,g550)
    c: Coincident(g550,g551)
    c: Coincident(g551,g552)
    c: Coincident(g552,g553)
    c: Coincident(g553,g554)
    c: Coincident(g554,g555)
    c: Coincident(g555,g556)
    c: Coincident(g556,g557)
    c: Coincident(g557,g558)
    c: Coincident(g558,g559)
    c: Coincident(g559,g560)
    c: Coincident(g560,g561)
    c: Coincident(g561,g562)
    c: Coincident(g562,g563)
    c: Coincident(g563,g564)
    c: Coincident(g564,g565)
    c: Coincident(g565,g566)
    c: Coincident(g566,g567)
    c: Coincident(g567,g568)
    c: Coincident(g568,g569)
    c: Coincident(g569,g570)
    c: Coincident(g570,g571)
    c: Coincident(g571,g572)
    c: Coincident(g572,g573)
    c: Coincident(g573,g574)
    c: Coincident(g574,g575)
    c: Coincident(g575,g576)
    c: Coincident(g576,g577)
    c: Coincident(g577,g578)
    c: Coincident(g578,g579)
    c: Coincident(g579,g580)
    c: Coincident(g580,g581)
    c: Coincident(g581,g582)
    c: Coincident(g582,g583)
    c: Coincident(g583,g584)
    c: Coincident(g584,g585)
    c: Coincident(g585,g586)
    c: Coincident(g586,g587)
    c: Coincident(g587,g588)
    c: Coincident(g588,g589)
    c: Coincident(g589,g590)
    c: Coincident(g590,g591)
    c: Coincident(g591,g592)
    c: Coincident(g592,g593)
    c: Coincident(g593,g594)
    c: Coincident(g594,g595)
    c: Coincident(g595,g596)
    c: Coincident(g596,g597)
    c: Coincident(g597,g598)
    c: Coincident(g598,g599)
    c: Coincident(g599,g600)
    c: Coincident(g600,g601)
    c: Coincident(g601,g602)
    c: Coincident(g602,g603)
    c: Coincident(g603,g604)
    c: Coincident(g604,g605)
    c: Coincident(g605,g606)
    c: Coincident(g606,g607)
    c: Coincident(g607,g608)
    c: Coincident(g608,g609)
    c: Coincident(g609,g610)
    c: Coincident(g610,g611)
    c: Coincident(g611,g612)
    c: Coincident(g612,g613)
    c: Coincident(g613,g614)
    c: Coincident(g614,g615)
    c: Coincident(g615,g616)
    c: Coincident(g616,g617)
    c: Coincident(g617,g618)
    c: Coincident(g618,g619)
    c: Coincident(g619,g620)
    c: Coincident(g620,g621)
    c: Coincident(g621,g622)
    c: Coincident(g622,g623)
    c: Coincident(g623,g624)
    c: Coincident(g624,g625)
    c: Coincident(g625,g626)
    c: Coincident(g626,g627)
    c: Coincident(g627,g317)
    c: Coincident(g628,g629)
    c: Coincident(g629,g630)
    c: Coincident(g630,g631)
    c: Coincident(g631,g632)
    c: Coincident(g632,g633)
    c: Coincident(g633,g634)
    c: Coincident(g634,g635)
    c: Coincident(g635,g636)
    c: Coincident(g636,g637)
    c: Coincident(g637,g638)
    c: Coincident(g638,g639)
    c: Coincident(g639,g640)
    c: Coincident(g640,g641)
    c: Coincident(g641,g642)
    c: Coincident(g642,g643)
    c: Coincident(g643,g644)
    c: Coincident(g644,g645)
    c: Coincident(g645,g646)
    c: Coincident(g646,g647)
    c: Coincident(g647,g648)
    c: Coincident(g648,g649)
    c: Coincident(g649,g650)
    c: Coincident(g650,g651)
    c: Coincident(g651,g652)
    c: Coincident(g652,g653)
    c: Coincident(g653,g654)
    c: Coincident(g654,g655)
    c: Coincident(g655,g656)
    c: Coincident(g656,g657)
    c: Coincident(g657,g658)
    c: Coincident(g658,g659)
    c: Coincident(g659,g660)
    c: Coincident(g660,g661)
    c: Coincident(g661,g662)
    c: Coincident(g662,g663)
    c: Coincident(g663,g664)
    c: Coincident(g664,g665)
    c: Coincident(g665,g666)
    c: Coincident(g666,g667)
    c: Coincident(g667,g668)
    c: Coincident(g668,g669)
    c: Coincident(g669,g670)
    c: Coincident(g670,g671)
    c: Coincident(g671,g672)
    c: Coincident(g672,g673)
    c: Coincident(g673,g674)
    c: Coincident(g674,g675)
    c: Coincident(g675,g676)
    c: Coincident(g676,g677)
    c: Coincident(g677,g678)
    c: Coincident(g678,g679)
    c: Coincident(g679,g680)
    c: Coincident(g680,g681)
    c: Coincident(g681,g682)
    c: Coincident(g682,g683)
    c: Coincident(g683,g684)
    c: Coincident(g684,g685)
    c: Coincident(g685,g686)
    c: Coincident(g686,g687)
    c: Coincident(g687,g688)
    c: Coincident(g688,g689)
    c: Coincident(g689,g690)
    c: Coincident(g690,g691)
    c: Coincident(g691,g692)
    c: Coincident(g692,g693)
    c: Coincident(g693,g694)
    c: Coincident(g694,g695)
    c: Coincident(g695,g696)
    c: Coincident(g696,g697)
    c: Coincident(g697,g698)
    c: Coincident(g698,g699)
    c: Coincident(g699,g700)
    c: Coincident(g700,g701)
    c: Coincident(g701,g702)
    c: Coincident(g702,g703)
    c: Coincident(g703,g704)
    c: Coincident(g704,g705)
    c: Coincident(g705,g706)
    c: Coincident(g706,g707)
    c: Coincident(g707,g708)
    c: Coincident(g708,g709)
    c: Coincident(g709,g710)
    c: Coincident(g710,g711)
    c: Coincident(g711,g712)
    c: Coincident(g712,g713)
    c: Coincident(g713,g714)
    c: Coincident(g714,g715)
    c: Coincident(g715,g716)
    c: Coincident(g716,g717)
    c: Coincident(g717,g718)
    c: Coincident(g718,g719)
    c: Coincident(g719,g720)
    c: Coincident(g720,g721)
    c: Coincident(g721,g722)
    c: Coincident(g722,g723)
    c: Coincident(g723,g724)
    c: Coincident(g724,g725)
    c: Coincident(g725,g726)
    c: Coincident(g726,g727)
    c: Coincident(g727,g728)
    c: Coincident(g728,g729)
    c: Coincident(g729,g730)
    c: Coincident(g730,g731)
    c: Coincident(g731,g732)
    c: Coincident(g732,g733)
    c: Coincident(g733,g734)
    c: Coincident(g734,g735)
    c: Coincident(g735,g736)
    c: Coincident(g736,g737)
    c: Coincident(g737,g738)
    c: Coincident(g738,g739)
    c: Coincident(g739,g740)
    c: Coincident(g740,g741)
    c: Coincident(g741,g742)
    c: Coincident(g742,g743)
    c: Coincident(g743,g744)
    c: Coincident(g744,g745)
    c: Coincident(g745,g746)
    c: Coincident(g746,g747)
    c: Coincident(g747,g748)
    c: Coincident(g748,g749)
    c: Coincident(g749,g750)
    c: Coincident(g750,g751)
    c: Coincident(g751,g752)
    c: Coincident(g752,g753)
    c: Coincident(g753,g754)
    c: Coincident(g754,g755)
    c: Coincident(g755,g756)
    c: Coincident(g756,g757)
    c: Coincident(g757,g758)
    c: Coincident(g758,g759)
    c: Coincident(g759,g760)
    c: Coincident(g760,g761)
    c: Coincident(g761,g762)
    c: Coincident(g762,g763)
    c: Coincident(g763,g764)
    c: Coincident(g764,g765)
    c: Coincident(g765,g766)
    c: Coincident(g766,g767)
    c: Coincident(g767,g768)
    c: Coincident(g768,g769)
    c: Coincident(g769,g770)
    c: Coincident(g770,g771)
    c: Coincident(g771,g772)
    c: Coincident(g772,g773)
    c: Coincident(g773,g774)
    c: Coincident(g774,g775)
    c: Coincident(g775,g776)
    c: Coincident(g776,g777)
    c: Coincident(g777,g778)
    c: Coincident(g778,g779)
    c: Coincident(g779,g780)
    c: Coincident(g780,g781)
    c: Coincident(g781,g782)
    c: Coincident(g782,g783)
    c: Coincident(g783,g784)
    c: Coincident(g784,g785)
    c: Coincident(g785,g786)
    c: Coincident(g786,g787)
    c: Coincident(g787,g788)
    c: Coincident(g788,g789)
    c: Coincident(g789,g790)
    c: Coincident(g790,g791)
    c: Coincident(g791,g792)
    c: Coincident(g792,g793)
    c: Coincident(g793,g794)
    c: Coincident(g794,g795)
    c: Coincident(g795,g796)
    c: Coincident(g796,g797)
    c: Coincident(g797,g798)
    c: Coincident(g798,g799)
    c: Coincident(g799,g800)
    c: Coincident(g800,g801)
    c: Coincident(g801,g802)
    c: Coincident(g802,g803)
    c: Coincident(g803,g804)
    c: Coincident(g804,g805)
    c: Coincident(g805,g806)
    c: Coincident(g806,g807)
    c: Coincident(g807,g808)
    c: Coincident(g808,g809)
    c: Coincident(g809,g810)
    c: Coincident(g810,g811)
    c: Coincident(g811,g812)
    c: Coincident(g812,g813)
    c: Coincident(g813,g814)
    c: Coincident(g814,g815)
    c: Coincident(g815,g816)
    c: Coincident(g816,g817)
    c: Coincident(g817,g818)
    c: Coincident(g818,g819)
    c: Coincident(g819,g820)
    c: Coincident(g820,g821)
    c: Coincident(g821,g822)
    c: Coincident(g822,g823)
    c: Coincident(g823,g824)
    c: Coincident(g824,g825)
    c: Coincident(g825,g826)
    c: Coincident(g826,g827)
    c: Coincident(g827,g828)
    c: Coincident(g828,g829)
    c: Coincident(g829,g830)
    c: Coincident(g830,g831)
    c: Coincident(g831,g832)
    c: Coincident(g832,g833)
    c: Coincident(g833,g834)
    c: Coincident(g834,g835)
    c: Coincident(g835,g836)
    c: Coincident(g836,g837)
    c: Coincident(g837,g838)
    c: Coincident(g838,g839)
    c: Coincident(g839,g840)
    c: Coincident(g840,g841)
    c: Coincident(g841,g842)
    c: Coincident(g842,g843)
    c: Coincident(g843,g844)
    c: Coincident(g844,g845)
    c: Coincident(g845,g846)
    c: Coincident(g846,g847)
    c: Coincident(g847,g848)
    c: Coincident(g848,g849)
    c: Coincident(g849,g850)
    c: Coincident(g850,g851)
    c: Coincident(g851,g852)
    c: Coincident(g852,g853)
    c: Coincident(g853,g854)
    c: Coincident(g854,g855)
    c: Coincident(g855,g856)
    c: Coincident(g856,g857)
    c: Coincident(g857,g858)
    c: Coincident(g858,g859)
    c: Coincident(g859,g860)
    c: Coincident(g860,g861)
    c: Coincident(g861,g862)
    c: Coincident(g862,g863)
    c: Coincident(g863,g864)
    c: Coincident(g864,g865)
    c: Coincident(g865,g866)
    c: Coincident(g866,g867)
    c: Coincident(g867,g868)
    c: Coincident(g868,g869)
    c: Coincident(g869,g870)
    c: Coincident(g870,g871)
    c: Coincident(g871,g872)
    c: Coincident(g872,g873)
    c: Coincident(g873,g874)
    c: Coincident(g874,g875)
    c: Coincident(g875,g876)
    c: Coincident(g876,g877)
    c: Coincident(g877,g878)
    c: Coincident(g878,g879)
    c: Coincident(g879,g880)
    c: Coincident(g880,g881)
    c: Coincident(g881,g882)
    c: Coincident(g882,g883)
    c: Coincident(g883,g884)
    c: Coincident(g884,g885)
    c: Coincident(g885,g886)
    c: Coincident(g886,g887)
    c: Coincident(g887,g888)
    c: Coincident(g888,g889)
    c: Coincident(g889,g890)
    c: Coincident(g890,g891)
    c: Coincident(g891,g892)
    c: Coincident(g892,g893)
    c: Coincident(g893,g894)
    c: Coincident(g894,g895)
    c: Coincident(g895,g896)
    c: Coincident(g896,g897)
    c: Coincident(g897,g898)
    c: Coincident(g898,g899)
    c: Coincident(g899,g900)
    c: Coincident(g900,g901)
    c: Coincident(g901,g902)
    c: Coincident(g902,g903)
    c: Coincident(g903,g904)
    c: Coincident(g904,g905)
    c: Coincident(g905,g906)
    c: Coincident(g906,g907)
    c: Coincident(g907,g908)
    c: Coincident(g908,g909)
    c: Coincident(g909,g910)
    c: Coincident(g910,g911)
    c: Coincident(g911,g912)
    c: Coincident(g912,g913)
    c: Coincident(g913,g914)
    c: Coincident(g914,g915)
    c: Coincident(g915,g916)
    c: Coincident(g916,g917)
    c: Coincident(g917,g918)
    c: Coincident(g918,g919)
    c: Coincident(g919,g920)
    c: Coincident(g920,g921)
    c: Coincident(g921,g922)
    c: Coincident(g922,g923)
    c: Coincident(g923,g924)
    c: Coincident(g924,g925)
    c: Coincident(g925,g926)
    c: Coincident(g926,g927)
    c: Coincident(g927,g928)
    c: Coincident(g928,g929)
    c: Coincident(g929,g930)
    c: Coincident(g930,g931)
    c: Coincident(g931,g932)
    c: Coincident(g932,g933)
    c: Coincident(g933,g934)
    c: Coincident(g934,g935)
    c: Coincident(g935,g936)
    c: Coincident(g936,g937)
    c: Coincident(g937,g938)
    c: Coincident(g938,g628)
    c: Coincident(g939,g940)
    c: Coincident(g940,g941)
    c: Coincident(g941,g942)
    c: Coincident(g942,g943)
    c: Coincident(g943,g944)
    c: Coincident(g944,g945)
    c: Coincident(g945,g946)
    c: Coincident(g946,g947)
    c: Coincident(g947,g948)
    c: Coincident(g948,g949)
    c: Coincident(g949,g950)
    c: Coincident(g950,g951)
    c: Coincident(g951,g952)
    c: Coincident(g952,g953)
    c: Coincident(g953,g954)
    c: Coincident(g954,g955)
    c: Coincident(g955,g956)
    c: Coincident(g956,g957)
    c: Coincident(g957,g958)
    c: Coincident(g958,g959)
    c: Coincident(g959,g960)
    c: Coincident(g960,g961)
    c: Coincident(g961,g962)
    c: Coincident(g962,g963)
    c: Coincident(g963,g964)
    c: Coincident(g964,g965)
    c: Coincident(g965,g966)
    c: Coincident(g966,g967)
    c: Coincident(g967,g968)
    c: Coincident(g968,g969)
    c: Coincident(g969,g970)
    c: Coincident(g970,g971)
    c: Coincident(g971,g972)
    c: Coincident(g972,g973)
    c: Coincident(g973,g974)
    c: Coincident(g974,g975)
    c: Coincident(g975,g976)
    c: Coincident(g976,g977)
    c: Coincident(g977,g978)
    c: Coincident(g978,g979)
    c: Coincident(g979,g980)
    c: Coincident(g980,g981)
    c: Coincident(g981,g982)
    c: Coincident(g982,g983)
    c: Coincident(g983,g984)
    c: Coincident(g984,g985)
    c: Coincident(g985,g986)
    c: Coincident(g986,g987)
    c: Coincident(g987,g988)
    c: Coincident(g988,g989)
    c: Coincident(g989,g990)
    c: Coincident(g990,g991)
    c: Coincident(g991,g992)
    c: Coincident(g992,g993)
    c: Coincident(g993,g994)
    c: Coincident(g994,g995)
    c: Coincident(g995,g996)
    c: Coincident(g996,g997)
    c: Coincident(g997,g998)
    c: Coincident(g998,g999)
    c: Coincident(g999,g1000)
    c: Coincident(g1000,g1001)
    c: Coincident(g1001,g1002)
    c: Coincident(g1002,g1003)
    c: Coincident(g1003,g1004)
    c: Coincident(g1004,g1005)
    c: Coincident(g1005,g1006)
    c: Coincident(g1006,g1007)
    c: Coincident(g1007,g1008)
    c: Coincident(g1008,g1009)
    c: Coincident(g1009,g1010)
    c: Coincident(g1010,g1011)
    c: Coincident(g1011,g1012)
    c: Coincident(g1012,g1013)
    c: Coincident(g1013,g1014)
    c: Coincident(g1014,g1015)
    c: Coincident(g1015,g1016)
    c: Coincident(g1016,g1017)
    c: Coincident(g1017,g1018)
    c: Coincident(g1018,g1019)
    c: Coincident(g1019,g1020)
    c: Coincident(g1020,g1021)
    c: Coincident(g1021,g1022)
    c: Coincident(g1022,g1023)
    c: Coincident(g1023,g1024)
    c: Coincident(g1024,g1025)
    c: Coincident(g1025,g1026)
    c: Coincident(g1026,g1027)
    c: Coincident(g1027,g1028)
    c: Coincident(g1028,g1029)
    c: Coincident(g1029,g1030)
    c: Coincident(g1030,g1031)
    c: Coincident(g1031,g1032)
    c: Coincident(g1032,g1033)
    c: Coincident(g1033,g1034)
    c: Coincident(g1034,g1035)
    c: Coincident(g1035,g1036)
    c: Coincident(g1036,g1037)
    c: Coincident(g1037,g1038)
    c: Coincident(g1038,g1039)
    c: Coincident(g1039,g1040)
    c: Coincident(g1040,g1041)
    c: Coincident(g1041,g1042)
    c: Coincident(g1042,g1043)
    c: Coincident(g1043,g1044)
    c: Coincident(g1044,g1045)
    c: Coincident(g1045,g1046)
    c: Coincident(g1046,g1047)
    c: Coincident(g1047,g1048)
    c: Coincident(g1048,g1049)
    c: Coincident(g1049,g1050)
    c: Coincident(g1050,g1051)
    c: Coincident(g1051,g1052)
    c: Coincident(g1052,g1053)
    c: Coincident(g1053,g1054)
    c: Coincident(g1054,g1055)
    c: Coincident(g1055,g1056)
    c: Coincident(g1056,g1057)
    c: Coincident(g1057,g1058)
    c: Coincident(g1058,g1059)
    c: Coincident(g1059,g1060)
    c: Coincident(g1060,g1061)
    c: Coincident(g1061,g1062)
    c: Coincident(g1062,g1063)
    c: Coincident(g1063,g1064)
    c: Coincident(g1064,g1065)
    c: Coincident(g1065,g1066)
    c: Coincident(g1066,g1067)
    c: Coincident(g1067,g1068)
    c: Coincident(g1068,g1069)
    c: Coincident(g1069,g1070)
    c: Coincident(g1070,g1071)
    c: Coincident(g1071,g1072)
    c: Coincident(g1072,g1073)
    c: Coincident(g1073,g1074)
    c: Coincident(g1074,g1075)
    c: Coincident(g1075,g1076)
    c: Coincident(g1076,g1077)
    c: Coincident(g1077,g1078)
    c: Coincident(g1078,g1079)
    c: Coincident(g1079,g1080)
    c: Coincident(g1080,g1081)
    c: Coincident(g1081,g1082)
    c: Coincident(g1082,g1083)
    c: Coincident(g1083,g1084)
    c: Coincident(g1084,g1085)
    c: Coincident(g1085,g1086)
    c: Coincident(g1086,g1087)
    c: Coincident(g1087,g1088)
    c: Coincident(g1088,g1089)
    c: Coincident(g1089,g1090)
    c: Coincident(g1090,g1091)
    c: Coincident(g1091,g1092)
    c: Coincident(g1092,g1093)
    c: Coincident(g1093,g1094)
    c: Coincident(g1094,g1095)
    c: Coincident(g1095,g1096)
    c: Coincident(g1096,g1097)
    c: Coincident(g1097,g1098)
    c: Coincident(g1098,g1099)
    c: Coincident(g1099,g1100)
    c: Coincident(g1100,g1101)
    c: Coincident(g1101,g1102)
    c: Coincident(g1102,g1103)
    c: Coincident(g1103,g1104)
    c: Coincident(g1104,g1105)
    c: Coincident(g1105,g1106)
    c: Coincident(g1106,g1107)
    c: Coincident(g1107,g1108)
    c: Coincident(g1108,g1109)
    c: Coincident(g1109,g1110)
    c: Coincident(g1110,g1111)
    c: Coincident(g1111,g1112)
    c: Coincident(g1112,g1113)
    c: Coincident(g1113,g1114)
    c: Coincident(g1114,g1115)
    c: Coincident(g1115,g1116)
    c: Coincident(g1116,g1117)
    c: Coincident(g1117,g1118)
    c: Coincident(g1118,g1119)
    c: Coincident(g1119,g1120)
    c: Coincident(g1120,g1121)
    c: Coincident(g1121,g1122)
    c: Coincident(g1122,g1123)
    c: Coincident(g1123,g1124)
    c: Coincident(g1124,g1125)
    c: Coincident(g1125,g1126)
    c: Coincident(g1126,g1127)
    c: Coincident(g1127,g1128)
    c: Coincident(g1128,g1129)
    c: Coincident(g1129,g1130)
    c: Coincident(g1130,g1131)
    c: Coincident(g1131,g1132)
    c: Coincident(g1132,g1133)
    c: Coincident(g1133,g1134)
    c: Coincident(g1134,g1135)
    c: Coincident(g1135,g1136)
    c: Coincident(g1136,g1137)
    c: Coincident(g1137,g1138)
    c: Coincident(g1138,g1139)
    c: Coincident(g1139,g1140)
    c: Coincident(g1140,g1141)
    c: Coincident(g1141,g1142)
    c: Coincident(g1142,g1143)
    c: Coincident(g1143,g1144)
    c: Coincident(g1144,g1145)
    c: Coincident(g1145,g1146)
    c: Coincident(g1146,g1147)
    c: Coincident(g1147,g1148)
    c: Coincident(g1148,g1149)
    c: Coincident(g1149,g1150)
    c: Coincident(g1150,g1151)
    c: Coincident(g1151,g1152)
    c: Coincident(g1152,g1153)
    c: Coincident(g1153,g1154)
    c: Coincident(g1154,g1155)
    c: Coincident(g1155,g1156)
    c: Coincident(g1156,g1157)
    c: Coincident(g1157,g1158)
    c: Coincident(g1158,g1159)
    c: Coincident(g1159,g1160)
    c: Coincident(g1160,g1161)
    c: Coincident(g1161,g1162)
    c: Coincident(g1162,g1163)
    c: Coincident(g1163,g1164)
    c: Coincident(g1164,g1165)
    c: Coincident(g1165,g1166)
    c: Coincident(g1166,g1167)
    c: Coincident(g1167,g1168)
    c: Coincident(g1168,g1169)
    c: Coincident(g1169,g1170)
    c: Coincident(g1170,g1171)
    c: Coincident(g1171,g1172)
    c: Coincident(g1172,g1173)
    c: Coincident(g1173,g1174)
    c: Coincident(g1174,g1175)
    c: Coincident(g1175,g1176)
    c: Coincident(g1176,g1177)
    c: Coincident(g1177,g1178)
    c: Coincident(g1178,g1179)
    c: Coincident(g1179,g1180)
    c: Coincident(g1180,g1181)
    c: Coincident(g1181,g1182)
    c: Coincident(g1182,g1183)
    c: Coincident(g1183,g1184)
    c: Coincident(g1184,g1185)
    c: Coincident(g1185,g1186)
    c: Coincident(g1186,g1187)
    c: Coincident(g1187,g1188)
    c: Coincident(g1188,g1189)
    c: Coincident(g1189,g1190)
    c: Coincident(g1190,g1191)
    c: Coincident(g1191,g1192)
    c: Coincident(g1192,g1193)
    c: Coincident(g1193,g1194)
    c: Coincident(g1194,g1195)
    c: Coincident(g1195,g1196)
    c: Coincident(g1196,g1197)
    c: Coincident(g1197,g1198)
    c: Coincident(g1198,g1199)
    c: Coincident(g1199,g1200)
    c: Coincident(g1200,g1201)
    c: Coincident(g1201,g1202)
    c: Coincident(g1202,g1203)
    c: Coincident(g1203,g1204)
    c: Coincident(g1204,g1205)
    c: Coincident(g1205,g1206)
    c: Coincident(g1206,g1207)
    c: Coincident(g1207,g1208)
    c: Coincident(g1208,g1209)
    c: Coincident(g1209,g1210)
    c: Coincident(g1210,g1211)
    c: Coincident(g1211,g1212)
    c: Coincident(g1212,g1213)
    c: Coincident(g1213,g1214)
    c: Coincident(g1214,g1215)
    c: Coincident(g1215,g1216)
    c: Coincident(g1216,g1217)
    c: Coincident(g1217,g1218)
    c: Coincident(g1218,g1219)
    c: Coincident(g1219,g1220)
    c: Coincident(g1220,g1221)
    c: Coincident(g1221,g1222)
    c: Coincident(g1222,g1223)
    c: Coincident(g1223,g1224)
    c: Coincident(g1224,g1225)
    c: Coincident(g1225,g1226)
    c: Coincident(g1226,g1227)
    c: Coincident(g1227,g1228)
    c: Coincident(g1228,g1229)
    c: Coincident(g1229,g1230)
    c: Coincident(g1230,g1231)
    c: Coincident(g1231,g1232)
    c: Coincident(g1232,g1233)
    c: Coincident(g1233,g1234)
    c: Coincident(g1234,g1235)
    c: Coincident(g1235,g1236)
    c: Coincident(g1236,g1237)
    c: Coincident(g1237,g1238)
    c: Coincident(g1238,g1239)
    c: Coincident(g1239,g1240)
    c: Coincident(g1240,g1241)
    c: Coincident(g1241,g1242)
    c: Coincident(g1242,g1243)
    c: Coincident(g1243,g1244)
    c: Coincident(g1244,g1245)
    c: Coincident(g1245,g1246)
    c: Coincident(g1246,g1247)
    c: Coincident(g1247,g1248)
    c: Coincident(g1248,g1249)
    c: Coincident(g1249,g939)
FEATURE [PartDesign::Pad] Pad
  Direction = (0,0,1)
  Length = 2
  Length2 = 10
  Placement = pos=(0,0,0) rot=(0,0,1;3.14159rad)
  Profile = -> Sketch
  ReferenceAxis = -> Sketch [N_Axis]
  Type = 0
FEATURE [PartDesign::Body] slot001
  Group = -> [LCS_001,Sketch,Pad]
  Origin = -> Origin001
  Tip = -> Pad
FEATURE [App::Part] slot
  Group = -> [LCS_0,slot001]
  Origin = -> Origin
FEATURE [Part::FeaturePython] Clone  label="slot002"  # Draft clone (typed FeaturePython)
  AttacherType = Attacher::AttachEngine3D
  Fuse = false
  Objects = -> [slot001]
  Placement = pos=(98,-2,1.2e-14) rot=(0,1,0;3.14159rad)
  Scale = (1,1,1)
